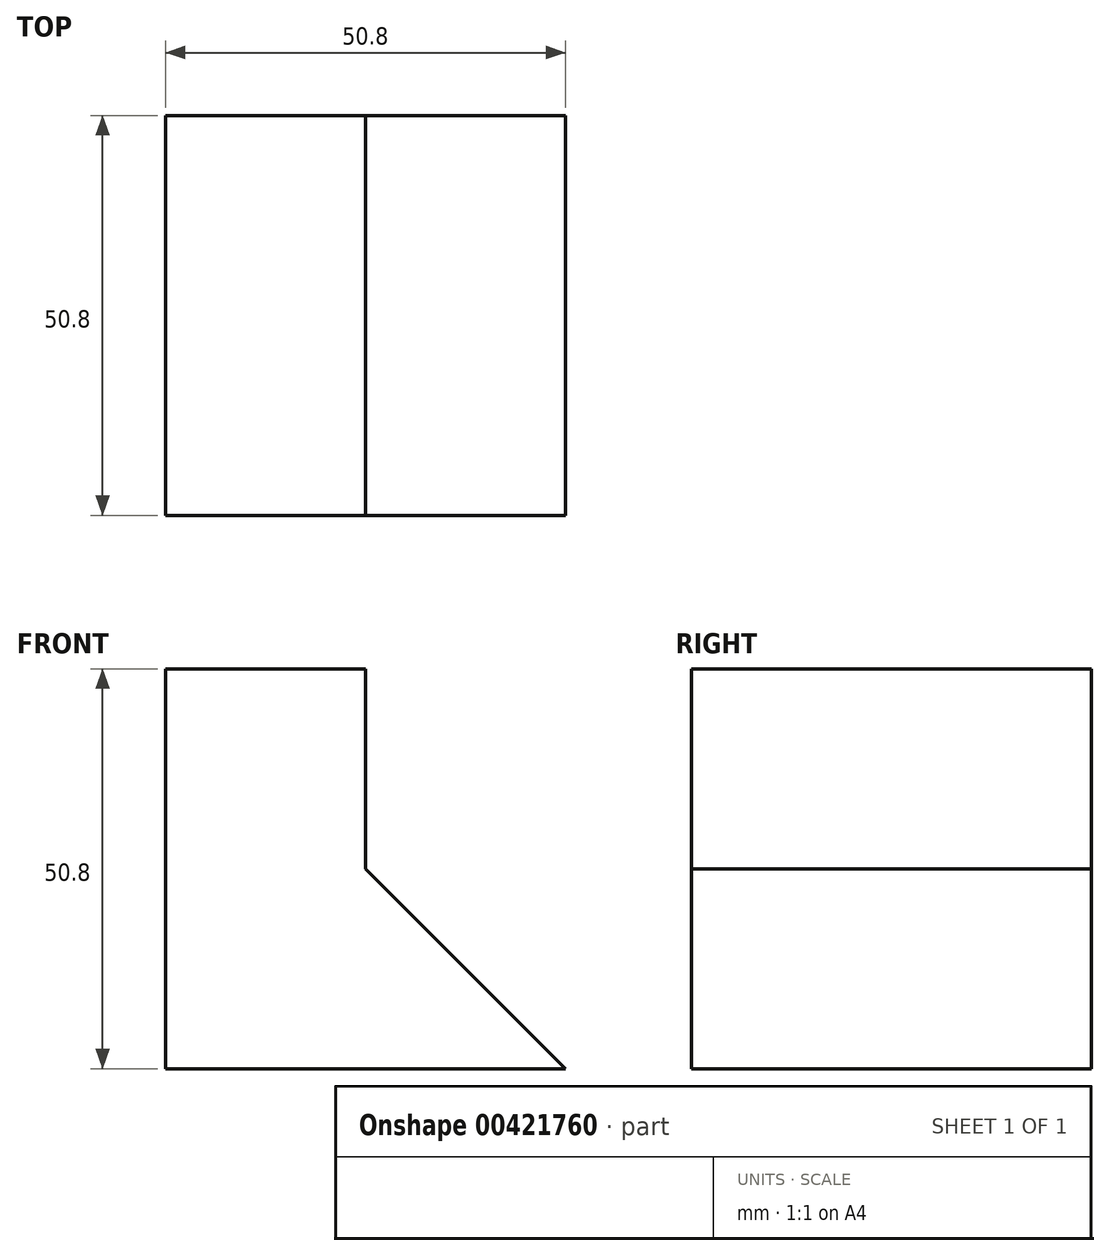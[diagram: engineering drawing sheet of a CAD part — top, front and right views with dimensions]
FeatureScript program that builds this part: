
annotation { "Feature Type Name" : "Feature", "Feature Type Description" : "" }
export const myFeature = defineFeature(function(context is Context, id is Id, definition is map)
    precondition{}
    {
        {
            var Q0;
            Q0=qCreatedBy(makeId("Front.planeOp"),FACE);
            var sketch = newSketch(context, id + "F0", { "sketchPlane" : qUnion([Q0])});
            skLineSegment(sketch, "E0", {"start": v(0, 0) * mm, "end": v(0, 50.8) * mm});
            skLineSegment(sketch, "E1", {"start": v(0, 50.8) * mm, "end": v(25.4, 50.8) * mm});
            skLineSegment(sketch, "E2", {"start": v(25.4, 50.8) * mm, "end": v(25.4, 25.4) * mm});
            skLineSegment(sketch, "E3", {"start": v(0, 0) * mm, "end": v(50.8, 0) * mm});
            skLineSegment(sketch, "E4", {"start": v(50.8, 0) * mm, "end": v(25.4, 25.4) * mm});
            skSolve(sketch);
        }
        {
            var Q0;
            Q0 = qSketchRegion(id + "F0", true);
            extrude(context, id + "F1", {"entities" : qUnion([Q0]), "depth" : 50.8 * mm});
        }
    });
